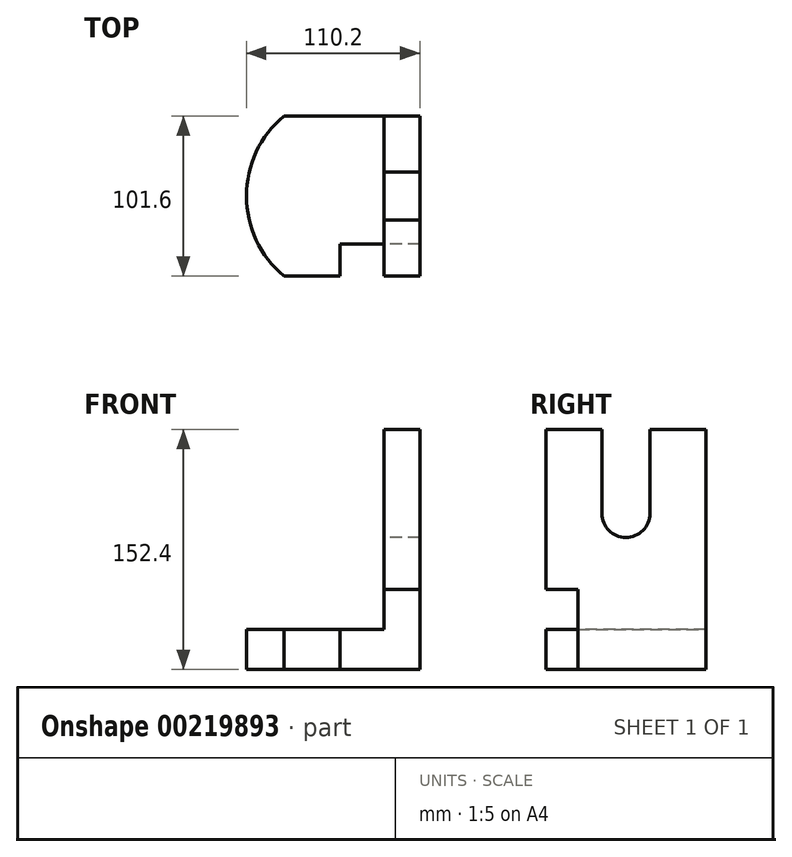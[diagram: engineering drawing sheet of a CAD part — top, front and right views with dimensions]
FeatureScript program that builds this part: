
annotation { "Feature Type Name" : "Feature", "Feature Type Description" : "" }
export const myFeature = defineFeature(function(context is Context, id is Id, definition is map)
    precondition{}
    {
        {
            var Q0;
            Q0=qCreatedBy(makeId("Front.planeOp"),FACE);
            var sketch = newSketch(context, id + "F0", { "sketchPlane" : qUnion([Q0])});
            skLineSegment(sketch, "E0.bottom", {"start": v(0, 152.4) * mm, "end": v(22.86, 152.4) * mm});
            skLineSegment(sketch, "E0.top", {"start": v(0, 0) * mm, "end": v(22.86, 0) * mm});
            skLineSegment(sketch, "E0.left", {"start": v(0, 152.4) * mm, "end": v(0, 25.4) * mm});
            skLineSegment(sketch, "E0.right", {"start": v(22.86, 152.4) * mm, "end": v(22.86, 0) * mm});
            skLineSegment(sketch, "E1.bottom", {"start": v(0, 25.4) * mm, "end": v(-88.9, 25.4) * mm});
            skLineSegment(sketch, "E1.top", {"start": v(0, 0) * mm, "end": v(-88.9, 0) * mm});
            skLineSegment(sketch, "E1.right", {"start": v(-88.9, 25.4) * mm, "end": v(-88.9, 0) * mm});
            skSolve(sketch);
        }
        {
            var Q0;
            Q0 = qSketchRegion(id + "F0", true);
            extrude(context, id + "F1", {"entities" : qUnion([Q0]), "depth" : 101.6 * mm});
        }
        {
            var Q0;
            Q0=makeQuery(id+"F1.opExtrude","SWEPT_FACE",FACE,{"disambiguationData":[OSD([sQuery(id+"F0.wireOp",EDGE,"E1.bottom")])]});
            var sketch = newSketch(context, id + "F2", { "sketchPlane" : qUnion([Q0])});
            skLineSegment(sketch, "E2.0", {"start": v(0, -101.6) * mm, "end": v(-88.9, -101.6) * mm});
            skLineSegment(sketch, "E3.0", {"start": v(0, 0) * mm, "end": v(-88.9, 0) * mm});
            skLineSegment(sketch, "E4.0", {"start": v(-88.9, -101.6) * mm, "end": v(-88.9, 0) * mm});
            skArc(sketch, "E5", {"start": v(-63.5, 0) * mm, "mid": v(-87.34, -50.8) * mm, "end": v(-63.5, -101.6) * mm});
            skSolve(sketch);
        }
        {
            var Q0;
            {var subQ0=sQuery(id+"F2.wireOp",EDGE,"E4.0");Q0=makeQuery(id+"F2.imprint","IMPRINT",FACE,{"disambiguationData":[TD([[makeQuery(id+"F2.imprint","IMPRINT",EDGE,{"derivedFrom":subQ0}),-1.0]])]});}
            extrude(context, id + "F3", {"entities" : qUnion([Q0]), "operationType" : NewBodyOperationType.REMOVE, "endBound" : BoundingType.THROUGH_ALL, "oppositeDirection" : true, "depth" : 25.4 * mm});
        }
        {
            var Q0;
            Q0=makeQuery(id+"F1.opExtrude","CAP_FACE",FACE,{"disambiguationData":[OSD([sQuery(id+"F0.wireOp",EDGE,"E0.bottom"),sQuery(id+"F0.wireOp",EDGE,"E0.top"),sQuery(id+"F0.wireOp",EDGE,"E0.left"),sQuery(id+"F0.wireOp",EDGE,"E0.right"),sQuery(id+"F0.wireOp",EDGE,"E1.bottom"),sQuery(id+"F0.wireOp",EDGE,"E1.top"),sQuery(id+"F0.wireOp",EDGE,"E1.right")])],"isStart":false});
            var sketch = newSketch(context, id + "F4", { "sketchPlane" : qUnion([Q0])});
            skLineSegment(sketch, "E6.bottom", {"start": v(22.86, 0) * mm, "end": v(-27.94, 0) * mm});
            skLineSegment(sketch, "E6.top", {"start": v(22.86, 50.8) * mm, "end": v(-27.94, 50.8) * mm});
            skLineSegment(sketch, "E6.left", {"start": v(22.86, 0) * mm, "end": v(22.86, 50.8) * mm});
            skLineSegment(sketch, "E6.right", {"start": v(-27.94, 0) * mm, "end": v(-27.94, 50.8) * mm});
            skSolve(sketch);
        }
        {
            var Q0;
            Q0 = qSketchRegion(id + "F4", true);
            extrude(context, id + "F5", {"entities" : qUnion([Q0]), "operationType" : NewBodyOperationType.REMOVE, "oppositeDirection" : true, "depth" : 20.32 * mm});
        }
        {
            var Q0;
            Q0=makeQuery(id+"F1.opExtrude","SWEPT_FACE",FACE,{"disambiguationData":[OSD([sQuery(id+"F0.wireOp",EDGE,"E0.left")])]});
            var sketch = newSketch(context, id + "F6", { "sketchPlane" : qUnion([Q0])});
            skLineSegment(sketch, "E7.bottom", {"start": v(35.56, 152.4) * mm, "end": v(66.04, 152.4) * mm});
            skLineSegment(sketch, "E7.left", {"start": v(35.56, 152.4) * mm, "end": v(35.56, 99.06) * mm});
            skLineSegment(sketch, "E7.right", {"start": v(66.04, 152.4) * mm, "end": v(66.04, 99.06) * mm});
            skArc(sketch, "E8", {"start": v(35.56, 99.06) * mm, "mid": v(50.8, 83.82) * mm, "end": v(66.04, 99.06) * mm});
            skPoint(sketch, "E8.centerSnap0", {"position": v(50.8, 152.4) * mm});
            skPoint(sketch, "E8.centerSnap1", {"position": v(50.8, 99.06) * mm});
            skSolve(sketch);
        }
        {
            var Q0;
            Q0=makeQuery(id+"F6.imprint","IMPRINT",FACE,{"disambiguationData":[TD([[makeQuery(id+"F6.imprint","IMPRINT",EDGE,{"derivedFrom":sQuery(id+"F6.wireOp",EDGE,"E7.bottom")}),1.0]])]});
            extrude(context, id + "F7", {"entities" : qUnion([Q0]), "operationType" : NewBodyOperationType.REMOVE, "endBound" : BoundingType.THROUGH_ALL, "oppositeDirection" : true, "depth" : 25.4 * mm});
        }
    });
